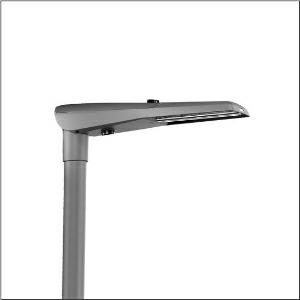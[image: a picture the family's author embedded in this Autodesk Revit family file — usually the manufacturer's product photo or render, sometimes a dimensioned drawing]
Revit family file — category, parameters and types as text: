
# Revit family: streetlight_sl_11_iq_mini___st1_2a_5xc2ac1y08he_5079
name_source: partatom
category: Lighting Fixtures
units: mm (PartAtom-declared; Revit-internal decimal feet)

## family parameters
Cut with Voids When Loaded = No
Host = Face
Light Source = No
Part Type = Normal
Room Calculation Point = No
Round Connector Dimension = Use Diameter
Shared = No

## types (1)
- --- (1 x LED, 6820 lm, 63.2 W, 2200K)
    Apparent Load = 63 VA
    CIE Flux Codes = 32 70 96 100 100
    Color Rendering = 70
    Color Temperature = 2200K
    Default Elevation = 1800 mm
    Description = Streetlight SL 11 iQ mini, mast luminaire, primary light control with 3 zone facetted reflector, of plastic, silver coated, highly specular, primary optical cover: cover, of PMMA, transparent, light distribution: ST1.2a, light emission: direct distribution, primary light characteristic: asymmetric, installation type: post-top, side-entry, lamps: LED, High Power LED, rated values: 8.070lm | 59,6W | 135,4lm/W (begin service life); end service life: 8.070lm | 62,8W; at 50% lumin. flux: 4.035lm | 28,3W | 142,6lm/W, colour temperature: 2200/2700/3000/4000K, colour rendering: CRI > 70, light colour: 722/727/730/740, light setting 1 begin service life: 100% | 8.070lm | 59,6W | 135,4lm/W | 3.000K, light setting 1 end service life: 62,8W, further light settings possible, control: pre-setting: logarithmic dimming characteristic, Street-Remote, Auto-Match, Temp-Guard, Lumen-Switch, Night-Set, Smart-Wire, Light-Fading, Desk-Remote (wireless, voltage-free reading and setting of iQ features in the workshop via application-optimized NFC function/RFID function), optimised constant luminous flux control (CLO 2.0), with cable H07RN-F 5x 1.5mm², mains connection: 230..240V, AC, 50/60Hz, connection cable pre-assembled, cable length: 8,5m, luminaire housing, of diecast aluminium, powder-coated, Siteco® metallic grey (DB 702S), please order mast flange separately, inclination adjustable without tools: 0°, 5°, 10°, 15° (post-top) | 0°, -5°, -10°, -15° (side-entry), sealing non-destructively replaceable, multi-level sealing system, length: 736mm, width: 174mm, height: 116mm, mast flange for spigot size: 42mm (side-entry): 5XC10008XM4, 60/48mm (side-entry/post-top): 5XC10108XM2, 76/60mm (side-entry/post-top): 5XC10108XM1, equipment: Power, Smart Interface below and above, protection rating (complete): IP66, insulation class (complete): insulation class II (safety insulation), certification: CE, ENEC, ENEC+, VDE, UKCA, impact resistance: IK10, permissible operating ambient temperature for outdoor applications: -25..+50°C, standard-compliant lighting for roads and squares, Environmental Product Declaration (EPD) tested and certified by an independent institute, packaging unit: 1 piece

Light Distribution: ST1.2a
    Height = 116 mm
    Lamp = 1 x LED
    Lamp Light Flux = 6820 lm
    Lamp Power = 63.2 W
    Lamp count = 1
    Length = 736 mm
    Luminous efficacy = 108 lm/W
    Manufacturer = Siteco
    ModVariant = No
    Model = 5XC2AC1Y08HE
    Number of Poles = 1
    OnlyDefault = Yes
    Power Factor = 1
    Product Name = Streetlight SL 11 iQ mini | ST1.2a
    Product group = mast luminaire | pylon top
    ProductGroupID = 6100
    Protection Class = Protection class II
    Protection Degree = IP 66
    RLX_Detail_Level = 1
    RLX_Emergency_Light_Flux = 0 lm
    RLX_Emergency_Type = 0
    RLX_Emergency_Type_DB = No
    RlxData = <blob elided: 54125 chars, md5=e4cb409d>
    Socket = socket
    Standby Power = 0 W
    System Light Flux = 6820 lm
    System Power = 63 W
    Type Comments = individual setting: luminous flux: 100 % | dim-lin: 254 | 866 mA
    Type Image = l_1006751.jpg
    URL = http://relux.com
    VarID = @adj_054997
    Voltage = 0 V
    Weight = 0.00 kg
    Width = 174 mm

## geometry (parser evidence)
native form markers: Blend x4, Sweep x11
no freeform markers — native parametric forms only
